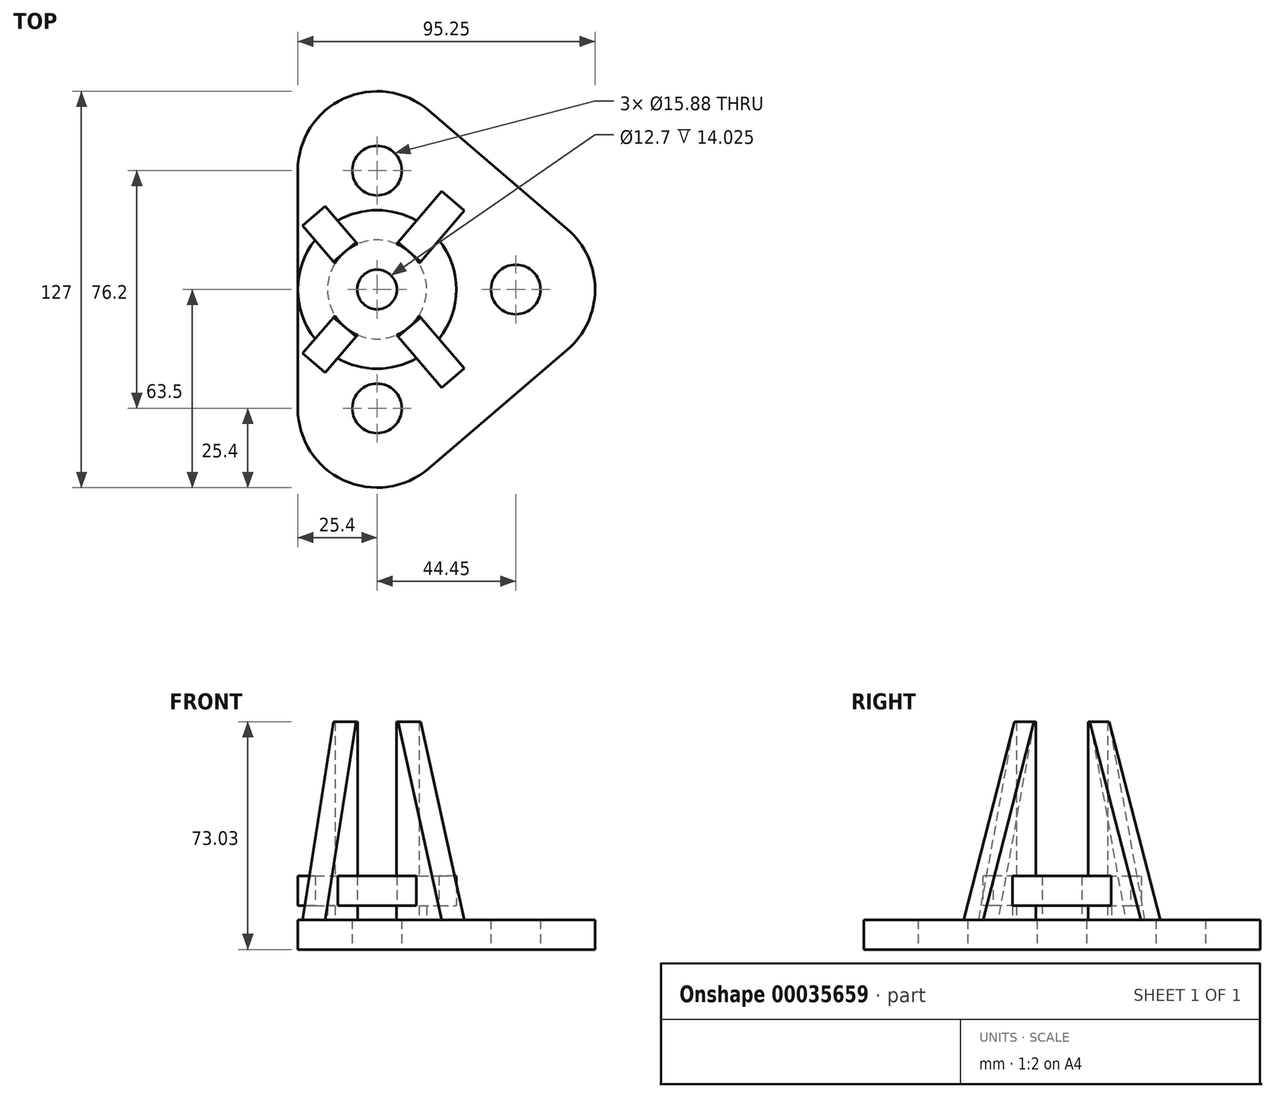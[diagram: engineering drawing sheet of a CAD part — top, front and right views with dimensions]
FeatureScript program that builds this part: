
annotation { "Feature Type Name" : "Feature", "Feature Type Description" : "" }
export const myFeature = defineFeature(function(context is Context, id is Id, definition is map)
    precondition{}
    {
        {
            var Q0;
            Q0=qCreatedBy(makeId("Top.planeOp"),FACE);
            var sketch = newSketch(context, id + "F0", { "sketchPlane" : qUnion([Q0])});
            skCircle(sketch, "E0", {"center": v(0, 0) * mm, "radius": 7.94 * mm});
            skCircle(sketch, "E1", {"center": v(-44.45, -38.1) * mm, "radius": 7.94 * mm});
            skCircle(sketch, "E2", {"center": v(-44.45, 38.1) * mm, "radius": 7.94 * mm});
            skArc(sketch, "E3", {"start": v(-69.85, -38.1) * mm, "mid": v(-55.06, -61.18) * mm, "end": v(-27.92, -57.39) * mm});
            skArc(sketch, "E4", {"start": v(-27.92, 57.39) * mm, "mid": v(-55.06, 61.18) * mm, "end": v(-69.85, 38.1) * mm});
            skArc(sketch, "E5", {"start": v(16.53, -19.29) * mm, "mid": v(25.4, 0) * mm, "end": v(16.53, 19.29) * mm});
            skLineSegment(sketch, "E6", {"start": v(-27.92, -57.39) * mm, "end": v(16.53, -19.29) * mm});
            skLineSegment(sketch, "E7", {"start": v(16.53, 19.29) * mm, "end": v(-27.92, 57.39) * mm});
            skLineSegment(sketch, "E8", {"start": v(-69.85, 38.1) * mm, "end": v(-69.85, -38.1) * mm});
            skSolve(sketch);
        }
        {
            var Q0;
            Q0=makeQuery(id+"F0.imprint","IMPRINT",FACE,{"disambiguationData":[TD([[makeQuery(id+"F0.imprint","IMPRINT",EDGE,{"derivedFrom":sQuery(id+"F0.wireOp",EDGE,"E0")}),-1.0]])]});
            extrude(context, id + "F1", {"entities" : qUnion([Q0]), "depth" : 9.52 * mm});
        }
        {
            var Q0;
            Q0=makeQuery(id+"F1.opExtrude","CAP_FACE",FACE,{"disambiguationData":[OSD([sQuery(id+"F0.wireOp",EDGE,"E0"),sQuery(id+"F0.wireOp",EDGE,"E1"),sQuery(id+"F0.wireOp",EDGE,"E2"),sQuery(id+"F0.wireOp",EDGE,"E3"),sQuery(id+"F0.wireOp",EDGE,"E4"),sQuery(id+"F0.wireOp",EDGE,"E5"),sQuery(id+"F0.wireOp",EDGE,"E6"),sQuery(id+"F0.wireOp",EDGE,"E7"),sQuery(id+"F0.wireOp",EDGE,"E8")])],"isStart":false});
            var sketch = newSketch(context, id + "F2", { "sketchPlane" : qUnion([Q0])});
            skCircle(sketch, "E9.0", {"center": v(-44.45, -38.1) * mm, "radius": 7.94 * mm});
            skCircle(sketch, "E10.0", {"center": v(-44.45, 38.1) * mm, "radius": 7.94 * mm});
            skLineSegment(sketch, "E11", {"start": v(-44.45, -38.1) * mm, "end": v(-44.45, 38.1) * mm, "construction": true});
            skCircle(sketch, "E12", {"center": v(-44.45, 0) * mm, "radius": 15.88 * mm});
            skCircle(sketch, "E13", {"center": v(-44.45, 0) * mm, "radius": 6.35 * mm});
            skSolve(sketch);
        }
        {
            var Q0;
            Q0=makeQuery(id+"F2.imprint","IMPRINT",FACE,{"disambiguationData":[TD([[makeQuery(id+"F2.imprint","IMPRINT",EDGE,{"derivedFrom":sQuery(id+"F2.wireOp",EDGE,"E12")}),1.0]])]});
            extrude(context, id + "F3", {"entities" : qUnion([Q0]), "operationType" : NewBodyOperationType.ADD, "depth" : (5 + 1 / 4 - 2 * (3 / 8)) * mm});
        }
        {
            var Q0;
            Q0=makeQuery(id+"F2.imprint","IMPRINT",FACE,{"disambiguationData":[TD([[makeQuery(id+"F2.imprint","IMPRINT",EDGE,{"derivedFrom":sQuery(id+"F2.wireOp",EDGE,"E9.0")}),-1.0]])]});
            var sketch = newSketch(context, id + "F4", { "sketchPlane" : qUnion([Q0])});
            skLineSegment(sketch, "E14.0", {"start": v(16.53, 19.29) * mm, "end": v(-27.92, 57.39) * mm});
            skCircle(sketch, "E15.0", {"center": v(-44.45, 0) * mm, "radius": 15.88 * mm});
            skLineSegment(sketch, "E16", {"start": v(-30.98, 8.4) * mm, "end": v(-16.51, 25.27) * mm});
            skLineSegment(sketch, "E17", {"start": v(-38.21, 14.6) * mm, "end": v(-23.75, 31.47) * mm});
            skLineSegment(sketch, "E18", {"start": v(-44.45, 0) * mm, "end": v(-9.1, 41.25) * mm, "construction": true});
            skLineSegment(sketch, "E19", {"start": v(-16.51, 25.27) * mm, "end": v(-23.75, 31.47) * mm});
            skLineSegment(sketch, "E20", {"start": v(-50.69, -14.6) * mm, "end": v(-61.02, -26.65) * mm});
            skLineSegment(sketch, "E21", {"start": v(-61.02, -26.65) * mm, "end": v(-68.25, -20.45) * mm});
            skLineSegment(sketch, "E22", {"start": v(-68.25, -20.45) * mm, "end": v(-57.92, -8.4) * mm});
            skSolve(sketch);
        }
        {
            var Q0;
            {var subQ1=sQuery(id+"F4.wireOp",EDGE,"E20");Q0=makeQuery(id+"F4.imprint","IMPRINT",FACE,{"disambiguationData":[TD([[makeQuery(id+"F4.imprint","IMPRINT",EDGE,{"derivedFrom":subQ1}),-1.0]])]});}
            var Q1;
            {var subQ1=sQuery(id+"F4.wireOp",EDGE,"E16");Q1=makeQuery(id+"F4.imprint","IMPRINT",FACE,{"disambiguationData":[TD([[makeQuery(id+"F4.imprint","IMPRINT",EDGE,{"derivedFrom":subQ1}),1.0]])]});}
            extrude(context, id + "F5", {"entities" : qUnion([Q0, Q1]), "depth" : 63.5 * mm});
        }
        {
            var Q0;
            Q0=makeQuery(id+"F5.opExtrude","SWEPT_FACE",FACE,{"disambiguationData":[OSD([sQuery(id+"F4.wireOp",EDGE,"E16")])]});
            var Q1;
            Q1=makeQuery(id+"F5.opExtrude","SWEPT_FACE",FACE,{"disambiguationData":[OSD([sQuery(id+"F4.wireOp",EDGE,"E17")])]});
            cPlane(context, id + "F6", {"entities" : qUnion([Q0, Q1]), "cplaneType" : CPlaneType.MID_PLANE, "offset" : 152.4 * mm, "width" : 152.4 * mm, "height" : 152.4 * mm});
        }
        {
            var Q0;
            Q0=qCreatedBy(id+"F6.planeOp",FACE);
            var sketch = newSketch(context, id + "F7", { "sketchPlane" : qUnion([Q0])});
            skLineSegment(sketch, "E23.0", {"start": v(-13.78, 73.03) * mm, "end": v(8.44, 73.03) * mm});
            skLineSegment(sketch, "E24.0", {"start": v(8.44, 73.03) * mm, "end": v(8.44, 9.53) * mm});
            skLineSegment(sketch, "E25.0", {"start": v(-59.95, 73.03) * mm, "end": v(-59.95, 9.53) * mm});
            skLineSegment(sketch, "E26.0", {"start": v(-44.8, 73.03) * mm, "end": v(-44.07, 73.03) * mm});
            skLineSegment(sketch, "E27.0", {"start": v(-44.07, 73.03) * mm, "end": v(-59.95, 73.03) * mm});
            skLineSegment(sketch, "E28", {"start": v(-59.95, 9.53) * mm, "end": v(-44.8, 73.03) * mm});
            skLineSegment(sketch, "E29.0", {"start": v(-13.78, 73.03) * mm, "end": v(-13.05, 73.03) * mm});
            skLineSegment(sketch, "E30", {"start": v(-13.05, 73.03) * mm, "end": v(8.44, 9.53) * mm});
            skSolve(sketch);
        }
        {
            var Q0;
            Q0 = qSketchRegion(id + "F7", true);
            extrude(context, id + "F8", {"entities" : qUnion([Q0]), "operationType" : NewBodyOperationType.REMOVE, "endBound" : BoundingType.THROUGH_ALL, "oppositeDirection" : true, "depth" : 25.4 * mm, "hasSecondDirection" : true, "secondDirectionBound" : SecondDirectionBoundingType.THROUGH_ALL, "secondDirectionOppositeDirection" : false, "secondDirectionDepth" : 25.4 * mm});
        }
        {
            var Q0;
            Q0=makeQuery(id+"F5.opExtrude","SWEPT_BODY",BODY,{"disambiguationData":[OSD([sQuery(id+"F4.wireOp",EDGE,"E15.0"),sQuery(id+"F4.wireOp",EDGE,"E20"),sQuery(id+"F4.wireOp",EDGE,"E21"),sQuery(id+"F4.wireOp",EDGE,"E22")])]});
            var Q1;
            Q1=makeQuery(id+"F5.opExtrude","SWEPT_BODY",BODY,{"disambiguationData":[OSD([sQuery(id+"F4.wireOp",EDGE,"E15.0"),sQuery(id+"F4.wireOp",EDGE,"E16"),sQuery(id+"F4.wireOp",EDGE,"E17"),sQuery(id+"F4.wireOp",EDGE,"E19")])]});
            var Q2;
            Q2=qCreatedBy(makeId("Front.planeOp"),FACE);
            mirror(context, id + "F9", {"operationType" : NewBodyOperationType.ADD, "entities" : qUnion([Q0, Q1]), "mirrorPlane" : qUnion([Q2])});
        }
        {
            var Q0;
            Q0=makeQuery(id+"F3.opExtrude","CAP_FACE",FACE,{"disambiguationData":[OSD([sQuery(id+"F2.wireOp",EDGE,"E12"),sQuery(id+"F2.wireOp",EDGE,"E13")])],"isStart":false});
            var sketch = newSketch(context, id + "F10", { "sketchPlane" : qUnion([Q0])});
            skCircle(sketch, "E31.0", {"center": v(-44.45, 0) * mm, "radius": 6.35 * mm});
            skCircle(sketch, "E32", {"center": v(-44.45, 0) * mm, "radius": 25.4 * mm});
            skSolve(sketch);
        }
        {
            var Q0;
            Q0=makeQuery(id+"F10.imprint","IMPRINT",FACE,{"disambiguationData":[TD([[makeQuery(id+"F10.imprint","IMPRINT",EDGE,{"derivedFrom":sQuery(id+"F10.wireOp",EDGE,"E32")}),1.0]])]});
            var Q1;
            Q1=makeQuery(id+"F10.imprint","IMPRINT",FACE,{"disambiguationData":[TD([[makeQuery(id+"F10.imprint","IMPRINT",EDGE,{"derivedFrom":sQuery(id+"F10.wireOp",EDGE,"E31.0")}),-1.0]])]});
            extrude(context, id + "F11", {"entities" : qUnion([Q0, Q1]), "operationType" : NewBodyOperationType.ADD, "depth" : 9.52 * mm});
        }
    });
